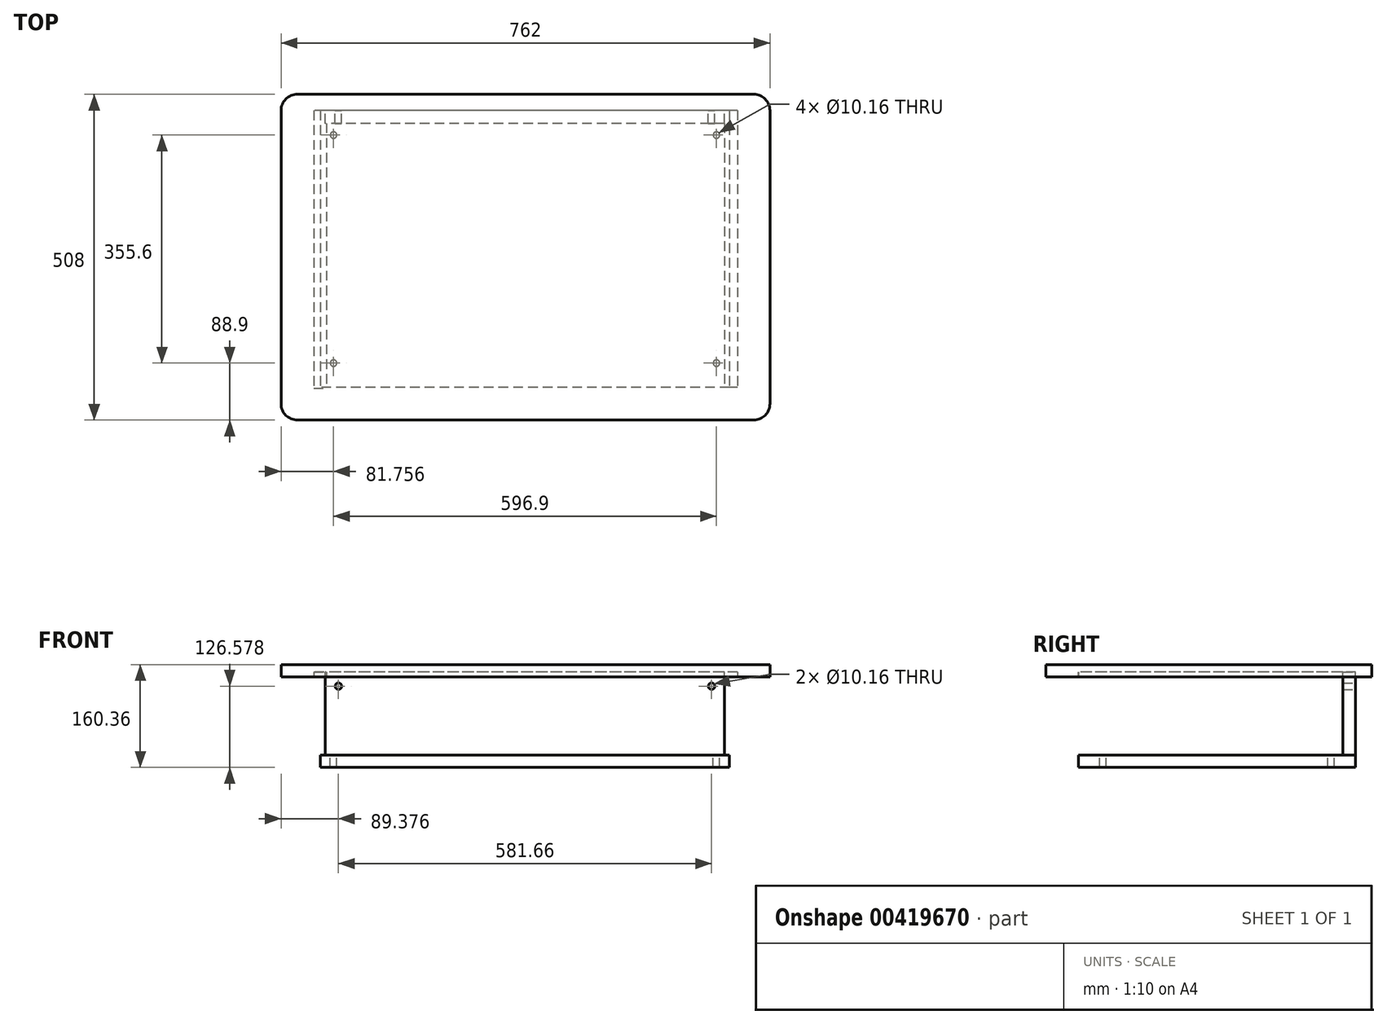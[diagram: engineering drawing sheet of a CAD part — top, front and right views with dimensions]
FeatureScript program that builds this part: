
annotation { "Feature Type Name" : "Feature", "Feature Type Description" : "" }
export const myFeature = defineFeature(function(context is Context, id is Id, definition is map)
    precondition{}
    {
        {
            var Q0;
            Q0=qCreatedBy(makeId("Top.planeOp"),FACE);
            var sketch = newSketch(context, id + "F0", { "sketchPlane" : qUnion([Q0])});
            skLineSegment(sketch, "E0.bottom", {"start": v(-355.6, 254) * mm, "end": v(355.6, 254) * mm});
            skLineSegment(sketch, "E0.top", {"start": v(-355.6, -254) * mm, "end": v(355.6, -254) * mm});
            skLineSegment(sketch, "E0.left", {"start": v(-381, 228.6) * mm, "end": v(-381, -228.6) * mm});
            skLineSegment(sketch, "E0.right", {"start": v(381, 228.6) * mm, "end": v(381, -228.6) * mm});
            skPoint(sketch, "E0.middle", {"position": v(0, 0) * mm});
            skPoint(sketch, "E1.visualSharp", {"position": v(381, 254) * mm});
            skArc(sketch, "E1.filletArc", {"start": v(381, 228.6) * mm, "mid": v(373.56, 246.56) * mm, "end": v(355.6, 254) * mm});
            skPoint(sketch, "E2.visualSharp", {"position": v(381, -254) * mm});
            skArc(sketch, "E2.filletArc", {"start": v(355.6, -254) * mm, "mid": v(373.56, -246.56) * mm, "end": v(381, -228.6) * mm});
            skPoint(sketch, "E3.visualSharp", {"position": v(-381, -254) * mm});
            skArc(sketch, "E3.filletArc", {"start": v(-381, -228.6) * mm, "mid": v(-373.56, -246.56) * mm, "end": v(-355.6, -254) * mm});
            skPoint(sketch, "E4.visualSharp", {"position": v(-381, 254) * mm});
            skArc(sketch, "E4.filletArc", {"start": v(-355.6, 254) * mm, "mid": v(-373.56, 246.56) * mm, "end": v(-381, 228.6) * mm});
            skSolve(sketch);
        }
        {
            var Q0;
            Q0=qSketchRegion(id+"F0",true);
            extrude(context, id + "F1", {"entities" : qUnion([Q0]), "depth" : 19.05 * mm, "offsetDistance" : 25.4 * mm});
        }
        {
            var Q0;
            Q0=makeQuery(id+"F1.opExtrude","CAP_FACE",FACE,{"disambiguationData":[OSD([sQuery(id+"F0.wireOp",EDGE,"E0.bottom"),sQuery(id+"F0.wireOp",EDGE,"E0.top"),sQuery(id+"F0.wireOp",EDGE,"E0.left"),sQuery(id+"F0.wireOp",EDGE,"E0.right"),sQuery(id+"F0.wireOp",EDGE,"E1.filletArc"),sQuery(id+"F0.wireOp",EDGE,"E2.filletArc"),sQuery(id+"F0.wireOp",EDGE,"E3.filletArc"),sQuery(id+"F0.wireOp",EDGE,"E4.filletArc")])],"isStart":true});
            var sketch = newSketch(context, id + "F2", { "sketchPlane" : qUnion([Q0])});
            skLineSegment(sketch, "E5.bottom", {"start": v(330.2, -228.6) * mm, "end": v(-330.2, -228.6) * mm});
            skLineSegment(sketch, "E5.top", {"start": v(330.2, -208.76) * mm, "end": v(-330.2, -208.76) * mm});
            skLineSegment(sketch, "E5.left", {"start": v(330.2, -228.6) * mm, "end": v(330.2, -208.76) * mm});
            skLineSegment(sketch, "E5.right", {"start": v(-330.2, -228.6) * mm, "end": v(-330.2, -208.76) * mm});
            skLineSegment(sketch, "E6.top", {"start": v(330.2, 203.2) * mm, "end": v(310.36, 203.2) * mm});
            skLineSegment(sketch, "E6.left", {"start": v(330.2, -208.76) * mm, "end": v(330.2, 203.2) * mm});
            skLineSegment(sketch, "E6.right", {"start": v(310.36, -209.55) * mm, "end": v(310.36, 203.2) * mm});
            skLineSegment(sketch, "E7.bottom", {"start": v(-330.2, -208.76) * mm, "end": v(-310.36, -208.76) * mm});
            skLineSegment(sketch, "E7.top", {"start": v(-330.2, 204) * mm, "end": v(-310.36, 204) * mm});
            skLineSegment(sketch, "E7.left", {"start": v(-330.2, -208.76) * mm, "end": v(-330.2, 204) * mm});
            skLineSegment(sketch, "E7.right", {"start": v(-310.36, -208.76) * mm, "end": v(-310.36, 204) * mm});
            skLineSegment(sketch, "E8", {"start": v(-320.28, 204) * mm, "end": v(-320.28, -228.6) * mm, "construction": true});
            skLineSegment(sketch, "E9", {"start": v(-330.2, -218.68) * mm, "end": v(330.2, -218.68) * mm, "construction": true});
            skLineSegment(sketch, "E10", {"start": v(320.28, 203.2) * mm, "end": v(320.28, -228.6) * mm, "construction": true});
            skSolve(sketch);
        }
        {
            var Q0;
            Q0=qSketchRegion(id+"F2",true);
            extrude(context, id + "F3", {"entities" : qUnion([Q0]), "operationType" : NewBodyOperationType.REMOVE, "oppositeDirection" : true, "depth" : 7.62 * mm});
        }
        {
            var Q0;
            Q0=makeQuery(id+"F3.boolean.opBoolean","COPY",FACE,{"derivedFrom":makeQuery(id+"F3.opExtrude","CAP_FACE",FACE,{"disambiguationData":[OSD([sQuery(id+"F2.wireOp",EDGE,"E5.bottom"),sQuery(id+"F2.wireOp",EDGE,"E5.top"),sQuery(id+"F2.wireOp",EDGE,"E5.left"),sQuery(id+"F2.wireOp",EDGE,"E5.right"),sQuery(id+"F2.wireOp",EDGE,"E6.top"),sQuery(id+"F2.wireOp",EDGE,"E6.left"),sQuery(id+"F2.wireOp",EDGE,"E6.right"),sQuery(id+"F2.wireOp",EDGE,"E7.top"),sQuery(id+"F2.wireOp",EDGE,"E7.left"),sQuery(id+"F2.wireOp",EDGE,"E7.right")])],"isStart":false})});
            var sketch = newSketch(context, id + "F4", { "sketchPlane" : qUnion([Q0])});
            skLineSegment(sketch, "E11.bottom", {"start": v(310.36, -208.76) * mm, "end": v(-311.94, -208.76) * mm});
            skLineSegment(sketch, "E11.top", {"start": v(310.36, -228.6) * mm, "end": v(-311.94, -228.6) * mm});
            skLineSegment(sketch, "E11.left", {"start": v(310.36, -208.76) * mm, "end": v(310.36, -228.6) * mm});
            skLineSegment(sketch, "E11.right", {"start": v(-311.94, -208.76) * mm, "end": v(-311.94, -228.6) * mm});
            skSolve(sketch);
        }
        {
            var Q0;
            Q0=makeQuery(id+"F4.imprint","IMPRINT",FACE,{"disambiguationData":[TD([[makeQuery(id+"F4.imprint","IMPRINT",EDGE,{"derivedFrom":sQuery(id+"F4.wireOp",EDGE,"E11.bottom")}),1.0]])]});
            extrude(context, id + "F5", {"entities" : qUnion([Q0]), "depth" : 129.88 * mm});
        }
        {
            var Q0;
            Q0=makeQuery(id+"F5.opExtrude","CAP_FACE",FACE,{"disambiguationData":[OSD([sQuery(id+"F4.wireOp",EDGE,"E11.bottom"),sQuery(id+"F4.wireOp",EDGE,"E11.top"),sQuery(id+"F4.wireOp",EDGE,"E11.left"),sQuery(id+"F4.wireOp",EDGE,"E11.right")])],"isStart":false});
            var sketch = newSketch(context, id + "F6", { "sketchPlane" : qUnion([Q0])});
            skLineSegment(sketch, "E12.bottom", {"start": v(317.98, -228.6) * mm, "end": v(-319.56, -228.6) * mm});
            skLineSegment(sketch, "E12.top", {"start": v(317.98, 203.2) * mm, "end": v(-319.56, 203.2) * mm});
            skLineSegment(sketch, "E12.left", {"start": v(317.98, -228.6) * mm, "end": v(317.98, 203.2) * mm});
            skLineSegment(sketch, "E12.right", {"start": v(-319.56, -228.6) * mm, "end": v(-319.56, 203.2) * mm});
            skSolve(sketch);
        }
        {
            var Q0;
            Q0=qSketchRegion(id+"F6",true);
            extrude(context, id + "F7", {"entities" : qUnion([Q0]), "depth" : 19.05 * mm});
        }
        {
            var Q0;
            Q0=makeQuery(id+"F5.opExtrude","SWEPT_FACE",FACE,{"disambiguationData":[OSD([sQuery(id+"F4.wireOp",EDGE,"E11.top")])]});
            var sketch = newSketch(context, id + "F8", { "sketchPlane" : qUnion([Q0])});
            skCircle(sketch, "E13", {"center": v(-290.04, -14.73) * mm, "radius": 5.08 * mm});
            skCircle(sketch, "E14", {"center": v(291.62, -14.73) * mm, "radius": 5.08 * mm});
            skSolve(sketch);
        }
        {
            var Q0;
            Q0 = qSketchRegion(id + "F8", true);
            extrude(context, id + "F9", {"entities" : qUnion([Q0]), "operationType" : NewBodyOperationType.REMOVE, "oppositeDirection" : true, "depth" : 25.4 * mm, "offsetDistance" : 25.4 * mm});
        }
        {
            var Q0;
            Q0=makeQuery(id+"F7.opExtrude","CAP_FACE",FACE,{"disambiguationData":[OSD([sQuery(id+"F6.wireOp",EDGE,"E12.bottom"),sQuery(id+"F6.wireOp",EDGE,"E12.top"),sQuery(id+"F6.wireOp",EDGE,"E12.left"),sQuery(id+"F6.wireOp",EDGE,"E12.right")])],"isStart":true});
            var sketch = newSketch(context, id + "F10", { "sketchPlane" : qUnion([Q0])});
            skCircle(sketch, "E15", {"center": v(-299.24, 190.5) * mm, "radius": 5.08 * mm});
            skCircle(sketch, "E16", {"center": v(297.66, 190.5) * mm, "radius": 5.08 * mm});
            skCircle(sketch, "E17", {"center": v(297.66, -165.1) * mm, "radius": 5.08 * mm});
            skCircle(sketch, "E18", {"center": v(-299.24, -165.1) * mm, "radius": 5.08 * mm});
            skSolve(sketch);
        }
        {
            var Q0;
            Q0 = qSketchRegion(id + "F10", true);
            extrude(context, id + "F11", {"entities" : qUnion([Q0]), "operationType" : NewBodyOperationType.REMOVE, "oppositeDirection" : true, "depth" : 25.4 * mm, "offsetDistance" : 25.4 * mm});
        }
    });
